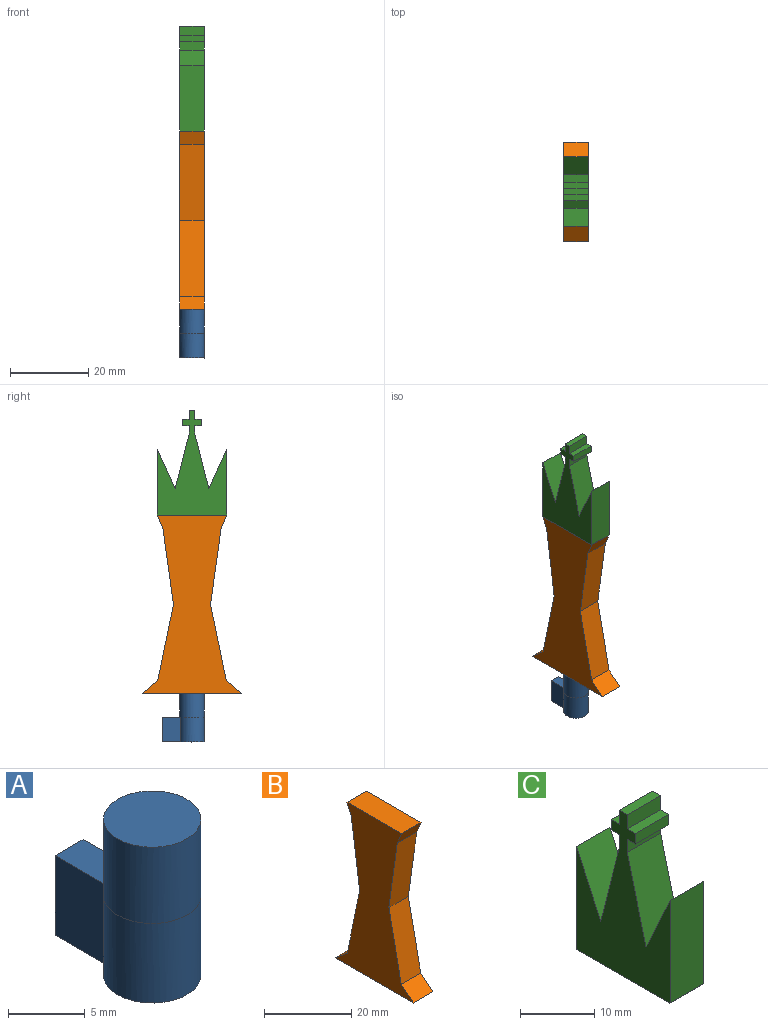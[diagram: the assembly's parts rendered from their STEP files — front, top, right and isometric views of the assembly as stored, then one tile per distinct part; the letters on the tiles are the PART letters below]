
ASSEMBLY  parts=3 mates=2
PART A: 8 faces, bbox 6.4x10.8x12.5 mm
  f0: plane 4.77x2.58mm, normal (0,0,1), area 11.8mm2, adj f1,f2,f4,f6
  f1: plane 6.35x2.58mm, normal (0,1,0), area 16.4mm2, adj f0,f2,f4,f5
  f2: plane 6.35x4.76mm, normal (-1,0,0), area 30.2mm2, adj f0,f1,f3,f5
  f3: cylinder r=3.17mm len=6.35mm, axis (0,0,-1), area 109.8mm2, adj f2,f4,f5,f6
  f4: plane 6.35x4.75mm, normal (1,0,0), area 30.2mm2, adj f0,f1,f3,f5
  f5: plane 10.83x6.35mm, normal (0,0,-1), area 43.5mm2, adj f1,f2,f3,f4
  f6: cylinder r=3.17mm len=6.35mm, axis (0,0,-1), area 121.6mm2, adj f0,f3,f7
  f7: plane 6.35x6.35mm, normal (0,0,1), area 31.7mm2, adj f6
PART B: 12 faces, bbox 6.3x25.4x45.7 mm
  f0: plane 17.73x6.32mm, normal (0,0,1), area 112.1mm2, adj f1,f2,f4,f8
  f1: plane 45.72x25.4mm, normal (1,0,0), area 628.2mm2, adj f0,f3,f4,f5,f6,f7,f8,f9
  f2: plane 45.72x25.4mm, normal (-1,0,0), area 628.2mm2, adj f0,f3,f4,f5,f6,f7,f8,f9
  f3: plane 25.4x6.32mm, normal (0,0,-1), area 160.6mm2, adj f1,f2,f7,f9
  f4: plane 6.32x3.34mm, normal (0,0.92,-0.39), area 22.9mm2, adj f0,f1,f2,f5
  f5: plane 19.52x6.32mm, normal (0,0.99,-0.14), area 124.7mm2, adj f1,f2,f4,f6
  f6: plane 19.55x6.32mm, normal (0,0.98,0.2), area 126.3mm2, adj f1,f2,f5,f7
  f7: plane 6.32x3.92mm, normal (0,0.65,0.76), area 32.4mm2, adj f1,f2,f3,f6
  f8: plane 6.32x3.34mm, normal (0,-0.92,-0.39), area 22.9mm2, adj f0,f1,f2,f11
  f9: plane 6.32x3.92mm, normal (0,-0.65,0.76), area 32.4mm2, adj f1,f2,f3,f10
  f10: plane 19.55x6.32mm, normal (0,-0.98,0.2), area 126.3mm2, adj f1,f2,f9,f11
  f11: plane 19.52x6.32mm, normal (0,-0.99,-0.14), area 124.7mm2, adj f1,f2,f8,f10
PART C: 24 faces, bbox 6.3x17.8x27 mm
  f0: plane 16.86x6.32mm, normal (0,-1,0), area 106.6mm2, adj f3,f4,f6,f23
  f1: plane 17.7x6.32mm, normal (0,0,-1), area 111.9mm2, adj f3,f4,f21,f22
  f2: plane 16.86x6.32mm, normal (0,1,0), area 106.6mm2, adj f3,f4,f7,f20
  f3: plane 26.95x17.78mm, normal (1,0,0), area 252.9mm2, adj f0,f1,f2,f5,f6,f7,f8,f9
  f4: plane 26.95x17.78mm, normal (-1,0,0), area 252.9mm2, adj f0,f1,f2,f5,f6,f7,f8,f9
  f5: plane 13.96x6.32mm, normal (0,0.97,0.25), area 91.1mm2, adj f3,f4,f7,f9
  f6: plane 10.07x6.32mm, normal (0,0.91,0.41), area 70mm2, adj f0,f3,f4,f8
  f7: plane 10.07x6.32mm, normal (0,-0.91,0.41), area 70mm2, adj f2,f3,f4,f5
  f8: plane 13.96x6.32mm, normal (0,-0.97,0.25), area 91.1mm2, adj f3,f4,f6,f12
  f9: plane 6.32x2.14mm, normal (0,1,0), area 13.5mm2, adj f3,f4,f5,f13
  f10: plane 6.32x1.71mm, normal (0,-1,0), area 10.8mm2, adj f3,f4,f11,f19
  f11: plane 6.32x1.56mm, normal (0,0,-1), area 9.9mm2, adj f3,f4,f10,f12
  f12: plane 6.32x2.14mm, normal (0,-1,0), area 13.5mm2, adj f3,f4,f8,f11
  f13: plane 6.32x1.56mm, normal (0,0,-1), area 9.9mm2, adj f3,f4,f9,f14
  f14: plane 6.32x1.71mm, normal (0,1,0), area 10.8mm2, adj f3,f4,f13,f15
  f15: plane 6.32x1.56mm, normal (0,0,1), area 9.9mm2, adj f3,f4,f14,f16
  f16: plane 6.32x2.32mm, normal (0,1,0), area 14.7mm2, adj f3,f4,f15,f17
  f17: plane 6.32x1.52mm, normal (0,0,1), area 9.6mm2, adj f3,f4,f16,f18
  f18: plane 6.32x2.32mm, normal (0,-1,0), area 14.7mm2, adj f3,f4,f17,f19
  f19: plane 6.32x1.56mm, normal (0,0,1), area 9.9mm2, adj f3,f4,f10,f18
  f20: plane 6.32x0.03mm, normal (0,0,-1), area 0.2mm2, adj f2,f3,f4,f21
  f21: plane 6.32x0.03mm, normal (0,0.92,-0.39), area 0.2mm2, adj f1,f3,f4,f20
  f22: plane 6.32x0.03mm, normal (0,-0.92,-0.39), area 0.2mm2, adj f1,f3,f4,f23
  f23: plane 6.32x0.03mm, normal (0,0,-1), area 0.2mm2, adj f0,f3,f4,f22
PLACE A t=(-1.37,-0.01,-28.33)mm
PLACE B t=(-1.37,-0.01,6.98)mm
PLACE C t=(-1.37,-0.01,7.01)mm
MATE fastened B.f0 <-> C.f1  axis (0,0,1) through (-1.37,-0.01,29.84)mm
MATE fastened B.f3 <-> A.f6  axis (0,0,-1) through (-1.37,-0.01,-15.88)mm
